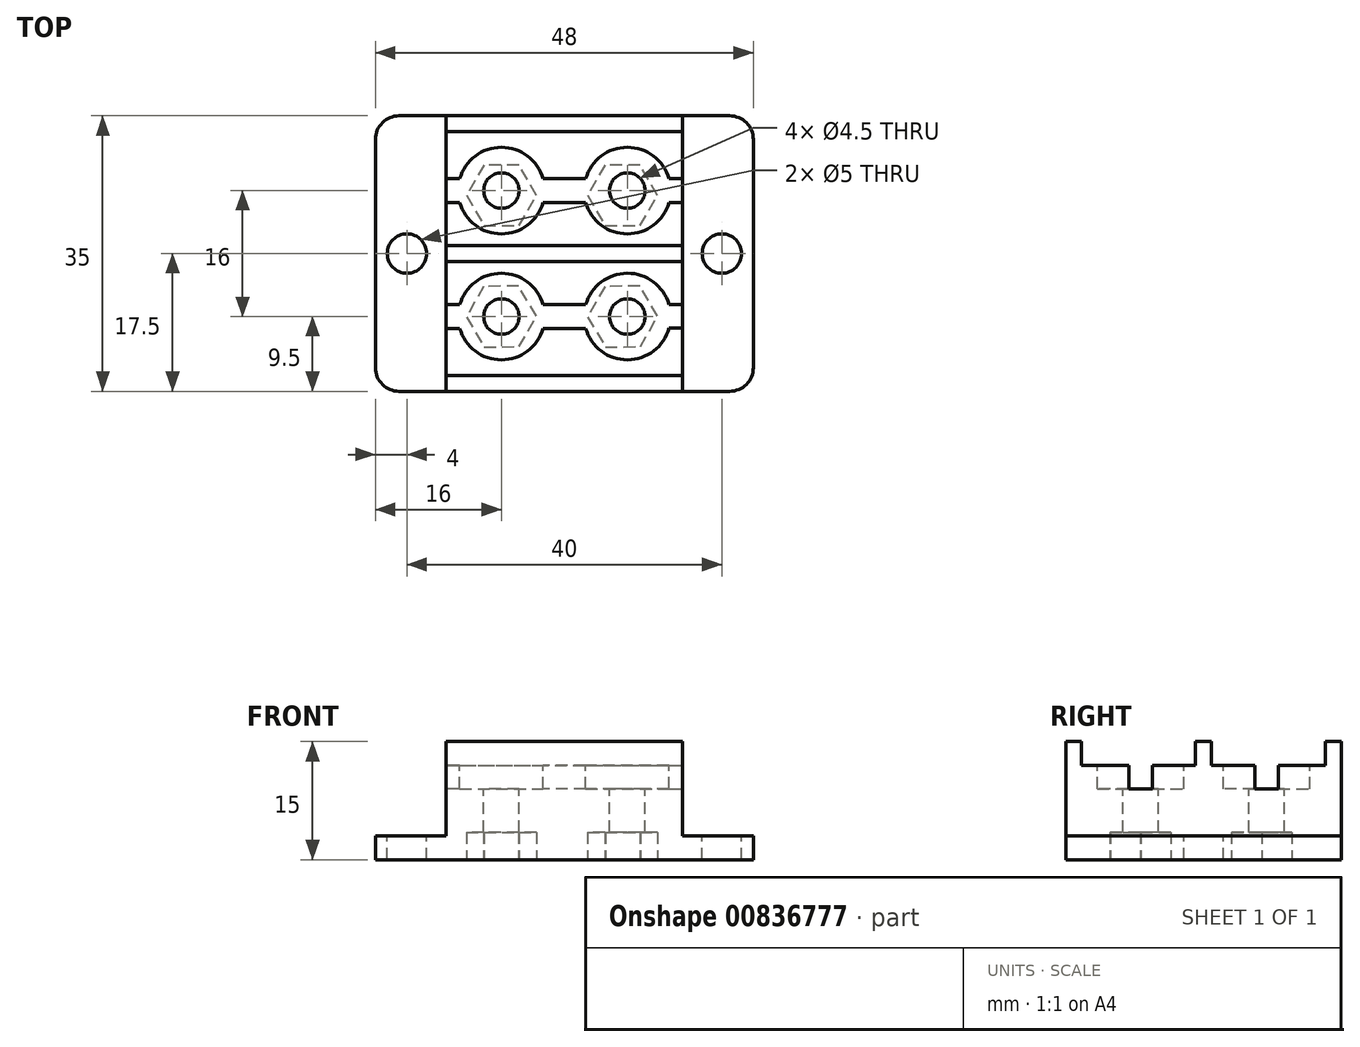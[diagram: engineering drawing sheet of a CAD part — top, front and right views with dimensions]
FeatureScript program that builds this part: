
annotation { "Feature Type Name" : "Feature", "Feature Type Description" : "" }
export const myFeature = defineFeature(function(context is Context, id is Id, definition is map)
    precondition{}
    {
        {
            var Q0;
            Q0=qCreatedBy(makeId("Front.planeOp"),FACE);
            var sketch = newSketch(context, id + "F0", { "sketchPlane" : qUnion([Q0])});
            skLineSegment(sketch, "E0", {"start": v(0, 0) * mm, "end": v(-9, 0) * mm});
            skLineSegment(sketch, "E1", {"start": v(-9, 0) * mm, "end": v(-9, 3) * mm});
            skLineSegment(sketch, "E2", {"start": v(-9, 3) * mm, "end": v(0, 3) * mm});
            skLineSegment(sketch, "E3", {"start": v(0, 3) * mm, "end": v(0, 12) * mm});
            skLineSegment(sketch, "E4", {"start": v(0, 12) * mm, "end": v(30, 12) * mm});
            skLineSegment(sketch, "E5", {"start": v(30, 12) * mm, "end": v(30, 3) * mm});
            skLineSegment(sketch, "E6", {"start": v(30, 3) * mm, "end": v(39, 3) * mm});
            skLineSegment(sketch, "E7", {"start": v(39, 3) * mm, "end": v(39, 0) * mm});
            skLineSegment(sketch, "E8", {"start": v(39, 0) * mm, "end": v(0, 0) * mm});
            skSolve(sketch);
        }
        {
            var Q0;
            Q0=makeQuery(id+"F0.imprint","IMPRINT",FACE,{"disambiguationData":[TD([[makeQuery(id+"F0.imprint","IMPRINT",EDGE,{"derivedFrom":sQuery(id+"F0.wireOp",EDGE,"E0")}),-1.0]])]});
            extrude(context, id + "F1", {"entities" : qUnion([Q0]), "oppositeDirection" : true, "depth" : 35 * mm, "offsetDistance" : 25 * mm});
        }
        {
            var Q0;
            Q0=qCreatedBy(makeId("Top.planeOp"),FACE);
            var Q1;
            Q1=makeQuery(id+"F1.opExtrude","CAP_VERTEX",VERTEX,{"disambiguationData":[OSD([sQuery(id+"F0.wireOp",EDGE,"E3"),sQuery(id+"F0.wireOp",EDGE,"E4")])],"isStart":false});
            cPlane(context, id + "F2", {"entities" : qUnion([Q0, Q1]), "cplaneType" : CPlaneType.PLANE_POINT, "offset" : 25 * mm, "width" : 150 * mm, "height" : 150 * mm});
        }
        {
            var Q0;
            Q0=qCreatedBy(id+"F2.planeOp",FACE);
            var sketch = newSketch(context, id + "F3", { "sketchPlane" : qUnion([Q0])});
            skLineSegment(sketch, "E9", {"start": v(23, 53.6) * mm, "end": v(23, -24.59) * mm, "construction": true});
            skLineSegment(sketch, "E10", {"start": v(7, 50.62) * mm, "end": v(7, -28.29) * mm, "construction": true});
            skLineSegment(sketch, "E11", {"start": v(23.6, 25.5) * mm, "end": v(1.01, 25.5) * mm, "construction": true});
            skLineSegment(sketch, "E12", {"start": v(28.02, 9.5) * mm, "end": v(4.88, 9.5) * mm, "construction": true});
            skCircle(sketch, "E13", {"center": v(23, 25.5) * mm, "radius": 2.25 * mm});
            skCircle(sketch, "E14", {"center": v(23, 9.5) * mm, "radius": 2.25 * mm});
            skCircle(sketch, "E15", {"center": v(7, 25.5) * mm, "radius": 2.25 * mm});
            skCircle(sketch, "E16", {"center": v(7, 9.5) * mm, "radius": 2.25 * mm});
            skLineSegment(sketch, "E17.bottom", {"start": v(29.45, 0) * mm, "end": v(0, 0) * mm});
            skLineSegment(sketch, "E18.bottom", {"start": v(8.68, 27) * mm, "end": v(21.32, 27) * mm});
            skLineSegment(sketch, "E18.top", {"start": v(8.68, 24) * mm, "end": v(21.32, 24) * mm});
            skLineSegment(sketch, "E18.left", {"start": v(8.68, 27) * mm, "end": v(8.68, 24) * mm});
            skLineSegment(sketch, "E18.right", {"start": v(21.32, 27) * mm, "end": v(21.32, 24) * mm});
            skLineSegment(sketch, "E19", {"start": v(8.68, 11) * mm, "end": v(21.32, 11) * mm});
            skLineSegment(sketch, "E20", {"start": v(21.32, 11) * mm, "end": v(21.32, 8) * mm});
            skLineSegment(sketch, "E21", {"start": v(21.32, 8) * mm, "end": v(8.68, 8) * mm});
            skLineSegment(sketch, "E22", {"start": v(8.68, 8) * mm, "end": v(8.68, 11) * mm});
            skCircle(sketch, "E23", {"center": v(7, 25.5) * mm, "radius": 5.5 * mm});
            skCircle(sketch, "E24", {"center": v(23, 25.5) * mm, "radius": 5.5 * mm});
            skCircle(sketch, "E25", {"center": v(7, 9.5) * mm, "radius": 5.5 * mm});
            skCircle(sketch, "E26", {"center": v(23, 9.5) * mm, "radius": 5.5 * mm});
            skLineSegment(sketch, "E27.bottom", {"start": v(28.3, 27) * mm, "end": v(30.07, 27) * mm});
            skLineSegment(sketch, "E28.bottom", {"start": v(5.32, 27) * mm, "end": v(0, 27) * mm});
            skLineSegment(sketch, "E28.top", {"start": v(5.32, 24) * mm, "end": v(0, 24) * mm});
            skLineSegment(sketch, "E28.left", {"start": v(5.32, 27) * mm, "end": v(5.32, 24) * mm});
            skLineSegment(sketch, "E28.right", {"start": v(0, 27) * mm, "end": v(0, 24) * mm});
            skLineSegment(sketch, "E29.bottom", {"start": v(24.68, 27) * mm, "end": v(30, 27) * mm});
            skLineSegment(sketch, "E29.top", {"start": v(24.68, 24) * mm, "end": v(30, 24) * mm});
            skLineSegment(sketch, "E29.left", {"start": v(24.68, 27) * mm, "end": v(24.68, 24) * mm});
            skLineSegment(sketch, "E29.right", {"start": v(30, 27) * mm, "end": v(30, 24) * mm});
            skLineSegment(sketch, "E30.bottom", {"start": v(5.32, 11) * mm, "end": v(0, 11) * mm});
            skLineSegment(sketch, "E30.top", {"start": v(5.32, 8) * mm, "end": v(0, 8) * mm});
            skLineSegment(sketch, "E30.left", {"start": v(5.32, 11) * mm, "end": v(5.32, 8) * mm});
            skLineSegment(sketch, "E30.right", {"start": v(0, 11) * mm, "end": v(0, 8) * mm});
            skLineSegment(sketch, "E31.bottom", {"start": v(24.64, 11.04) * mm, "end": v(30, 11.04) * mm});
            skLineSegment(sketch, "E31.top", {"start": v(24.64, 8.04) * mm, "end": v(30, 8.04) * mm});
            skLineSegment(sketch, "E31.left", {"start": v(24.64, 11.04) * mm, "end": v(24.64, 8.04) * mm});
            skLineSegment(sketch, "E31.right", {"start": v(30, 11.04) * mm, "end": v(30, 8.04) * mm});
            skSolve(sketch);
        }
        {
            var Q0;
            Q0=makeQuery(id+"F1.opExtrude","SWEPT_FACE",FACE,{"disambiguationData":[OSD([sQuery(id+"F0.wireOp",EDGE,"E6")])]});
            var sketch = newSketch(context, id + "F4", { "sketchPlane" : qUnion([Q0])});
            skCircle(sketch, "E32", {"center": v(-5, 17.5) * mm, "radius": 2.5 * mm});
            skCircle(sketch, "E33", {"center": v(35, 17.5) * mm, "radius": 2.5 * mm});
            skSolve(sketch);
        }
        {
            var Q0;
            Q0=makeQuery(id+"F4.imprint","IMPRINT",FACE,{"disambiguationData":[TD([[makeQuery(id+"F4.imprint","IMPRINT",EDGE,{"derivedFrom":sQuery(id+"F4.wireOp",EDGE,"E32")}),1.0]])]});
            var Q1;
            Q1=makeQuery(id+"F4.imprint","IMPRINT",FACE,{"disambiguationData":[TD([[makeQuery(id+"F4.imprint","IMPRINT",EDGE,{"derivedFrom":sQuery(id+"F4.wireOp",EDGE,"E33")}),1.0]])]});
            extrude(context, id + "F5", {"entities" : qUnion([Q0, Q1]), "operationType" : NewBodyOperationType.REMOVE, "endBound" : BoundingType.UP_TO_NEXT, "oppositeDirection" : true, "depth" : 25 * mm, "offsetDistance" : 25 * mm});
        }
        {
            var Q0;
            Q0=makeQuery(id+"F1.opExtrude","CAP_EDGE",EDGE,{"disambiguationData":[OSD([sQuery(id+"F0.wireOp",EDGE,"E1")])],"isStart":false});
            var Q1;
            Q1=makeQuery(id+"F1.opExtrude","CAP_EDGE",EDGE,{"disambiguationData":[OSD([sQuery(id+"F0.wireOp",EDGE,"E7")])],"isStart":false});
            var Q2;
            Q2=makeQuery(id+"F1.opExtrude","CAP_EDGE",EDGE,{"disambiguationData":[OSD([sQuery(id+"F0.wireOp",EDGE,"E7")])],"isStart":true});
            var Q3;
            Q3=makeQuery(id+"F1.opExtrude","CAP_EDGE",EDGE,{"disambiguationData":[OSD([sQuery(id+"F0.wireOp",EDGE,"E1")])],"isStart":true});
            fillet(context, id + "F6", {"entities" : qUnion([Q0, Q1, Q2, Q3]), "radius" : 3 * mm, "tangentPropagation" : true, "allowEdgeOverflow" : false});
        }
        {
            var Q0;
            Q0=makeQuery(id+"F1.opExtrude","SWEPT_FACE",FACE,{"disambiguationData":[OSD([sQuery(id+"F0.wireOp",EDGE,"E4")])]});
            var sketch = newSketch(context, id + "F7", { "sketchPlane" : qUnion([Q0])});
            skLineSegment(sketch, "E34.bottom", {"start": v(0, 35) * mm, "end": v(30, 35) * mm});
            skLineSegment(sketch, "E34.top", {"start": v(0, 33) * mm, "end": v(30, 33) * mm});
            skLineSegment(sketch, "E34.left", {"start": v(0, 35) * mm, "end": v(0, 33) * mm});
            skLineSegment(sketch, "E34.right", {"start": v(30, 35) * mm, "end": v(30, 33) * mm});
            skLineSegment(sketch, "E35.bottom", {"start": v(0, 18.5) * mm, "end": v(30, 18.5) * mm});
            skLineSegment(sketch, "E35.top", {"start": v(0, 16.5) * mm, "end": v(30, 16.5) * mm});
            skLineSegment(sketch, "E35.left", {"start": v(0, 18.5) * mm, "end": v(0, 16.5) * mm});
            skLineSegment(sketch, "E35.right", {"start": v(30, 18.5) * mm, "end": v(30, 16.5) * mm});
            skLineSegment(sketch, "E36.bottom", {"start": v(0, 0) * mm, "end": v(30, 0) * mm});
            skLineSegment(sketch, "E36.top", {"start": v(0, 2) * mm, "end": v(30, 2) * mm});
            skLineSegment(sketch, "E36.left", {"start": v(0, 0) * mm, "end": v(0, 2) * mm});
            skLineSegment(sketch, "E36.right", {"start": v(30, 0) * mm, "end": v(30, 2) * mm});
            skSolve(sketch);
        }
        {
            var Q0;
            Q0=makeQuery(id+"F7.imprint","IMPRINT",FACE,{"disambiguationData":[TD([[makeQuery(id+"F7.imprint","IMPRINT",EDGE,{"derivedFrom":sQuery(id+"F7.wireOp",EDGE,"E34.bottom")}),-1.0]])]});
            var Q1;
            Q1=makeQuery(id+"F7.imprint","IMPRINT",FACE,{"disambiguationData":[TD([[makeQuery(id+"F7.imprint","IMPRINT",EDGE,{"derivedFrom":sQuery(id+"F7.wireOp",EDGE,"E35.bottom")}),-1.0]])]});
            var Q2;
            Q2=makeQuery(id+"F7.imprint","IMPRINT",FACE,{"disambiguationData":[TD([[makeQuery(id+"F7.imprint","IMPRINT",EDGE,{"derivedFrom":sQuery(id+"F7.wireOp",EDGE,"E36.bottom")}),1.0]])]});
            extrude(context, id + "F8", {"entities" : qUnion([Q0, Q1, Q2]), "operationType" : NewBodyOperationType.ADD, "depth" : 3 * mm, "offsetDistance" : 25 * mm});
        }
        {
            var Q0;
            {var subQ0=sQuery(id+"F3.wireOp",EDGE,"E18.left");Q0=makeQuery(id+"F3.imprint","IMPRINT",FACE,{"disambiguationData":[TD([[makeQuery(id+"F3.imprint","IMPRINT",EDGE,{"derivedFrom":subQ0}),-1.0]])]});}
            var Q1;
            {var subQ0=sQuery(id+"F3.wireOp",EDGE,"E28.left");Q1=makeQuery(id+"F3.imprint","IMPRINT",FACE,{"disambiguationData":[TD([[makeQuery(id+"F3.imprint","IMPRINT",EDGE,{"derivedFrom":subQ0}),-1.0]])]});}
            var Q2;
            {var subQ0=sQuery(id+"F3.wireOp",EDGE,"E18.left");Q2=makeQuery(id+"F3.imprint","IMPRINT",FACE,{"disambiguationData":[TD([[makeQuery(id+"F3.imprint","IMPRINT",EDGE,{"derivedFrom":subQ0}),1.0]])]});}
            var Q3;
            {var subQ0=sQuery(id+"F3.wireOp",EDGE,"E18.right");Q3=makeQuery(id+"F3.imprint","IMPRINT",FACE,{"disambiguationData":[TD([[makeQuery(id+"F3.imprint","IMPRINT",EDGE,{"derivedFrom":subQ0}),-1.0]])]});}
            var Q4;
            {var subQ0=sQuery(id+"F3.wireOp",EDGE,"E29.left");Q4=makeQuery(id+"F3.imprint","IMPRINT",FACE,{"disambiguationData":[TD([[makeQuery(id+"F3.imprint","IMPRINT",EDGE,{"derivedFrom":subQ0}),1.0]])]});}
            var Q5;
            {var subQ0=sQuery(id+"F3.wireOp",EDGE,"E18.right");Q5=makeQuery(id+"F3.imprint","IMPRINT",FACE,{"disambiguationData":[TD([[makeQuery(id+"F3.imprint","IMPRINT",EDGE,{"derivedFrom":subQ0}),1.0]])]});}
            var Q6;
            {var subQ0=sQuery(id+"F3.wireOp",EDGE,"E22");Q6=makeQuery(id+"F3.imprint","IMPRINT",FACE,{"disambiguationData":[TD([[makeQuery(id+"F3.imprint","IMPRINT",EDGE,{"derivedFrom":subQ0}),1.0]])]});}
            var Q7;
            {var subQ0=sQuery(id+"F3.wireOp",EDGE,"E22");Q7=makeQuery(id+"F3.imprint","IMPRINT",FACE,{"disambiguationData":[TD([[makeQuery(id+"F3.imprint","IMPRINT",EDGE,{"derivedFrom":subQ0}),-1.0]])]});}
            var Q8;
            {var subQ0=sQuery(id+"F3.wireOp",EDGE,"E30.left");Q8=makeQuery(id+"F3.imprint","IMPRINT",FACE,{"disambiguationData":[TD([[makeQuery(id+"F3.imprint","IMPRINT",EDGE,{"derivedFrom":subQ0}),-1.0]])]});}
            var Q9;
            {var subQ0=sQuery(id+"F3.wireOp",EDGE,"E20");Q9=makeQuery(id+"F3.imprint","IMPRINT",FACE,{"disambiguationData":[TD([[makeQuery(id+"F3.imprint","IMPRINT",EDGE,{"derivedFrom":subQ0}),-1.0]])]});}
            var Q10;
            {var subQ0=sQuery(id+"F3.wireOp",EDGE,"E31.left");Q10=makeQuery(id+"F3.imprint","IMPRINT",FACE,{"disambiguationData":[TD([[makeQuery(id+"F3.imprint","IMPRINT",EDGE,{"derivedFrom":subQ0}),1.0]])]});}
            var Q11;
            {var subQ4=sQuery(id+"F3.wireOp",EDGE,"E20");Q11=makeQuery(id+"F3.imprint","IMPRINT",FACE,{"disambiguationData":[TD([[makeQuery(id+"F3.imprint","IMPRINT",EDGE,{"derivedFrom":subQ4}),1.0]])]});}
            extrude(context, id + "F9", {"entities" : qUnion([Q0, Q1, Q2, Q3, Q4, Q5, Q6, Q7, Q8, Q9, Q10, Q11]), "operationType" : NewBodyOperationType.REMOVE, "endBound" : BoundingType.UP_TO_NEXT, "oppositeDirection" : true, "depth" : 25 * mm, "offsetDistance" : 25 * mm});
        }
        {
            var Q0;
            {var subQ0=sQuery(id+"F3.wireOp",EDGE,"E21");var subQ5=sQuery(id+"F3.wireOp",EDGE,"E25");var subQ6=makeQuery(id+"F3.imprint","INTERSECT",VERTEX,{"derivedFrom":[subQ0,subQ5]});Q0=makeQuery(id+"F3.imprint","IMPRINT",FACE,{"disambiguationData":[TD([[makeQuery(id+"F3.imprint","IMPRINT",EDGE,{"disambiguationData":[TD([[subQ6,1.0]])],"derivedFrom":subQ5}),1.0]])]});}
            var Q1;
            {var subQ1=sQuery(id+"F3.wireOp",EDGE,"E30.bottom");var subQ6=sQuery(id+"F3.wireOp",EDGE,"E25");var subQ7=makeQuery(id+"F3.imprint","INTERSECT",VERTEX,{"derivedFrom":[subQ6,subQ1]});Q1=makeQuery(id+"F3.imprint","IMPRINT",FACE,{"disambiguationData":[TD([[makeQuery(id+"F3.imprint","IMPRINT",EDGE,{"disambiguationData":[TD([[subQ7,-1.0]])],"derivedFrom":subQ6}),1.0]])]});}
            var Q2;
            {var subQ0=sQuery(id+"F3.wireOp",EDGE,"E19");var subQ5=sQuery(id+"F3.wireOp",EDGE,"E25");var subQ6=makeQuery(id+"F3.imprint","INTERSECT",VERTEX,{"derivedFrom":[subQ0,subQ5]});Q2=makeQuery(id+"F3.imprint","IMPRINT",FACE,{"disambiguationData":[TD([[makeQuery(id+"F3.imprint","IMPRINT",EDGE,{"disambiguationData":[TD([[subQ6,-1.0]])],"derivedFrom":subQ5}),1.0]])]});}
            var Q3;
            {var subQ1=sQuery(id+"F3.wireOp",EDGE,"E19");var subQ6=sQuery(id+"F3.wireOp",EDGE,"E25");var subQ8=makeQuery(id+"F3.imprint","INTERSECT",VERTEX,{"derivedFrom":[subQ1,subQ6]});Q3=makeQuery(id+"F3.imprint","IMPRINT",FACE,{"disambiguationData":[TD([[makeQuery(id+"F3.imprint","IMPRINT",EDGE,{"disambiguationData":[TD([[subQ8,1.0]])],"derivedFrom":subQ6}),1.0]])]});}
            var Q4;
            {var subQ0=sQuery(id+"F3.wireOp",EDGE,"E19");var subQ5=sQuery(id+"F3.wireOp",EDGE,"E26");var subQ6=makeQuery(id+"F3.imprint","INTERSECT",VERTEX,{"derivedFrom":[subQ0,subQ5]});Q4=makeQuery(id+"F3.imprint","IMPRINT",FACE,{"disambiguationData":[TD([[makeQuery(id+"F3.imprint","IMPRINT",EDGE,{"disambiguationData":[TD([[subQ6,1.0]])],"derivedFrom":subQ5}),1.0]])]});}
            var Q5;
            {var subQ1=sQuery(id+"F3.wireOp",EDGE,"E19");var subQ6=sQuery(id+"F3.wireOp",EDGE,"E26");var subQ7=makeQuery(id+"F3.imprint","INTERSECT",VERTEX,{"derivedFrom":[subQ1,subQ6]});Q5=makeQuery(id+"F3.imprint","IMPRINT",FACE,{"disambiguationData":[TD([[makeQuery(id+"F3.imprint","IMPRINT",EDGE,{"disambiguationData":[TD([[subQ7,-1.0]])],"derivedFrom":subQ6}),1.0]])]});}
            var Q6;
            {var subQ0=sQuery(id+"F3.wireOp",EDGE,"E21");var subQ5=sQuery(id+"F3.wireOp",EDGE,"E26");var subQ6=makeQuery(id+"F3.imprint","INTERSECT",VERTEX,{"derivedFrom":[subQ0,subQ5]});Q6=makeQuery(id+"F3.imprint","IMPRINT",FACE,{"disambiguationData":[TD([[makeQuery(id+"F3.imprint","IMPRINT",EDGE,{"disambiguationData":[TD([[subQ6,-1.0]])],"derivedFrom":subQ5}),1.0]])]});}
            var Q7;
            {var subQ0=sQuery(id+"F3.wireOp",EDGE,"E31.bottom");var subQ5=sQuery(id+"F3.wireOp",EDGE,"E26");var subQ6=makeQuery(id+"F3.imprint","INTERSECT",VERTEX,{"derivedFrom":[subQ5,subQ0]});Q7=makeQuery(id+"F3.imprint","IMPRINT",FACE,{"disambiguationData":[TD([[makeQuery(id+"F3.imprint","IMPRINT",EDGE,{"disambiguationData":[TD([[subQ6,1.0]])],"derivedFrom":subQ5}),1.0]])]});}
            var Q8;
            {var subQ0=sQuery(id+"F3.wireOp",EDGE,"E18.top");var subQ5=sQuery(id+"F3.wireOp",EDGE,"E24");var subQ6=makeQuery(id+"F3.imprint","INTERSECT",VERTEX,{"derivedFrom":[subQ0,subQ5]});Q8=makeQuery(id+"F3.imprint","IMPRINT",FACE,{"disambiguationData":[TD([[makeQuery(id+"F3.imprint","IMPRINT",EDGE,{"disambiguationData":[TD([[subQ6,-1.0]])],"derivedFrom":subQ5}),1.0]])]});}
            var Q9;
            {var subQ1=sQuery(id+"F3.wireOp",EDGE,"E29.bottom");var subQ6=sQuery(id+"F3.wireOp",EDGE,"E24");var subQ7=makeQuery(id+"F3.imprint","INTERSECT",VERTEX,{"derivedFrom":[subQ6,subQ1]});Q9=makeQuery(id+"F3.imprint","IMPRINT",FACE,{"disambiguationData":[TD([[makeQuery(id+"F3.imprint","IMPRINT",EDGE,{"disambiguationData":[TD([[subQ7,1.0]])],"derivedFrom":subQ6}),1.0]])]});}
            var Q10;
            {var subQ0=sQuery(id+"F3.wireOp",EDGE,"E18.bottom");var subQ5=sQuery(id+"F3.wireOp",EDGE,"E24");var subQ6=makeQuery(id+"F3.imprint","INTERSECT",VERTEX,{"derivedFrom":[subQ0,subQ5]});Q10=makeQuery(id+"F3.imprint","IMPRINT",FACE,{"disambiguationData":[TD([[makeQuery(id+"F3.imprint","IMPRINT",EDGE,{"disambiguationData":[TD([[subQ6,1.0]])],"derivedFrom":subQ5}),1.0]])]});}
            var Q11;
            {var subQ1=sQuery(id+"F3.wireOp",EDGE,"E18.bottom");var subQ6=sQuery(id+"F3.wireOp",EDGE,"E24");var subQ8=makeQuery(id+"F3.imprint","INTERSECT",VERTEX,{"derivedFrom":[subQ1,subQ6]});Q11=makeQuery(id+"F3.imprint","IMPRINT",FACE,{"disambiguationData":[TD([[makeQuery(id+"F3.imprint","IMPRINT",EDGE,{"disambiguationData":[TD([[subQ8,-1.0]])],"derivedFrom":subQ6}),1.0]])]});}
            var Q12;
            {var subQ0=sQuery(id+"F3.wireOp",EDGE,"E18.top");var subQ5=sQuery(id+"F3.wireOp",EDGE,"E23");var subQ7=makeQuery(id+"F3.imprint","INTERSECT",VERTEX,{"derivedFrom":[subQ0,subQ5]});Q12=makeQuery(id+"F3.imprint","IMPRINT",FACE,{"disambiguationData":[TD([[makeQuery(id+"F3.imprint","IMPRINT",EDGE,{"disambiguationData":[TD([[subQ7,1.0]])],"derivedFrom":subQ5}),1.0]])]});}
            var Q13;
            {var subQ0=sQuery(id+"F3.wireOp",EDGE,"E18.bottom");var subQ5=sQuery(id+"F3.wireOp",EDGE,"E23");var subQ7=makeQuery(id+"F3.imprint","INTERSECT",VERTEX,{"derivedFrom":[subQ0,subQ5]});Q13=makeQuery(id+"F3.imprint","IMPRINT",FACE,{"disambiguationData":[TD([[makeQuery(id+"F3.imprint","IMPRINT",EDGE,{"disambiguationData":[TD([[subQ7,-1.0]])],"derivedFrom":subQ5}),1.0]])]});}
            var Q14;
            {var subQ1=sQuery(id+"F3.wireOp",EDGE,"E18.bottom");var subQ6=sQuery(id+"F3.wireOp",EDGE,"E23");var subQ7=makeQuery(id+"F3.imprint","INTERSECT",VERTEX,{"derivedFrom":[subQ1,subQ6]});Q14=makeQuery(id+"F3.imprint","IMPRINT",FACE,{"disambiguationData":[TD([[makeQuery(id+"F3.imprint","IMPRINT",EDGE,{"disambiguationData":[TD([[subQ7,1.0]])],"derivedFrom":subQ6}),1.0]])]});}
            var Q15;
            {var subQ1=sQuery(id+"F3.wireOp",EDGE,"E28.bottom");var subQ6=sQuery(id+"F3.wireOp",EDGE,"E23");var subQ7=makeQuery(id+"F3.imprint","INTERSECT",VERTEX,{"derivedFrom":[subQ6,subQ1]});Q15=makeQuery(id+"F3.imprint","IMPRINT",FACE,{"disambiguationData":[TD([[makeQuery(id+"F3.imprint","IMPRINT",EDGE,{"disambiguationData":[TD([[subQ7,-1.0]])],"derivedFrom":subQ6}),1.0]])]});}
            extrude(context, id + "F10", {"entities" : qUnion([Q0, Q1, Q2, Q3, Q4, Q5, Q6, Q7, Q8, Q9, Q10, Q11, Q12, Q13, Q14, Q15]), "operationType" : NewBodyOperationType.REMOVE, "oppositeDirection" : true, "depth" : 3 * mm, "offsetDistance" : 25 * mm});
        }
        {
            var Q0;
            Q0=qSketchRegion(id+"F3",true);
            extrude(context, id + "F11", {"entities" : qUnion([Q0]), "operationType" : NewBodyOperationType.REMOVE, "oppositeDirection" : true, "depth" : 3 * mm, "offsetDistance" : 25 * mm});
        }
        {
            var Q0;
            Q0=makeQuery(id+"F1.opExtrude","SWEPT_FACE",FACE,{"disambiguationData":[OSD([sQuery(id+"F0.wireOp",EDGE,"E0"),sQuery(id+"F0.wireOp",EDGE,"E8")])]});
            var sketch = newSketch(context, id + "F12", { "sketchPlane" : qUnion([Q0])});
            skCircle(sketch, "E37.cCircle", {"center": v(7, -9.5) * mm, "radius": 3.85 * mm, "construction": true});
            skLineSegment(sketch, "E37.0", {"start": v(11.45, -9.54) * mm, "end": v(9.2, -13.37) * mm});
            skLineSegment(sketch, "E37.1", {"start": v(9.2, -13.37) * mm, "end": v(4.75, -13.33) * mm});
            skLineSegment(sketch, "E37.2", {"start": v(4.75, -13.33) * mm, "end": v(2.55, -9.46) * mm});
            skLineSegment(sketch, "E37.3", {"start": v(2.55, -9.46) * mm, "end": v(4.8, -5.63) * mm});
            skLineSegment(sketch, "E37.4", {"start": v(4.8, -5.63) * mm, "end": v(9.25, -5.67) * mm});
            skLineSegment(sketch, "E37.5", {"start": v(9.25, -5.67) * mm, "end": v(11.45, -9.54) * mm});
            skPoint(sketch, "E37.0.midPoint", {"position": v(10.32, -11.45) * mm});
            skCircle(sketch, "E38.cCircle", {"center": v(22.4, -9.5) * mm, "radius": 3.85 * mm, "construction": true});
            skLineSegment(sketch, "E38.0", {"start": v(26.85, -9.54) * mm, "end": v(24.6, -13.37) * mm});
            skLineSegment(sketch, "E38.1", {"start": v(24.6, -13.37) * mm, "end": v(20.15, -13.33) * mm});
            skLineSegment(sketch, "E38.2", {"start": v(20.15, -13.33) * mm, "end": v(17.95, -9.46) * mm});
            skLineSegment(sketch, "E38.3", {"start": v(17.95, -9.46) * mm, "end": v(20.2, -5.63) * mm});
            skLineSegment(sketch, "E38.4", {"start": v(20.2, -5.63) * mm, "end": v(24.65, -5.67) * mm});
            skLineSegment(sketch, "E38.5", {"start": v(24.65, -5.67) * mm, "end": v(26.85, -9.54) * mm});
            skPoint(sketch, "E38.0.midPoint", {"position": v(25.72, -11.45) * mm});
            skCircle(sketch, "E39.cCircle", {"center": v(7, -24.9) * mm, "radius": 3.85 * mm, "construction": true});
            skLineSegment(sketch, "E39.0", {"start": v(11.45, -24.9) * mm, "end": v(9.22, -28.75) * mm});
            skLineSegment(sketch, "E39.1", {"start": v(9.22, -28.75) * mm, "end": v(4.78, -28.75) * mm});
            skLineSegment(sketch, "E39.2", {"start": v(4.78, -28.75) * mm, "end": v(2.55, -24.9) * mm});
            skLineSegment(sketch, "E39.3", {"start": v(2.55, -24.9) * mm, "end": v(4.78, -21.05) * mm});
            skLineSegment(sketch, "E39.4", {"start": v(4.78, -21.05) * mm, "end": v(9.22, -21.05) * mm});
            skLineSegment(sketch, "E39.5", {"start": v(9.22, -21.05) * mm, "end": v(11.45, -24.9) * mm});
            skPoint(sketch, "E39.0.midPoint", {"position": v(10.33, -26.82) * mm});
            skCircle(sketch, "E40.cCircle", {"center": v(22.4, -24.9) * mm, "radius": 3.85 * mm, "construction": true});
            skLineSegment(sketch, "E40.0", {"start": v(26.85, -24.9) * mm, "end": v(24.62, -28.75) * mm});
            skLineSegment(sketch, "E40.1", {"start": v(24.62, -28.75) * mm, "end": v(20.18, -28.75) * mm});
            skLineSegment(sketch, "E40.2", {"start": v(20.18, -28.75) * mm, "end": v(17.95, -24.9) * mm});
            skLineSegment(sketch, "E40.3", {"start": v(17.95, -24.9) * mm, "end": v(20.18, -21.05) * mm});
            skLineSegment(sketch, "E40.4", {"start": v(20.18, -21.05) * mm, "end": v(24.62, -21.05) * mm});
            skLineSegment(sketch, "E40.5", {"start": v(24.62, -21.05) * mm, "end": v(26.85, -24.9) * mm});
            skPoint(sketch, "E40.0.midPoint", {"position": v(25.73, -26.82) * mm});
            skSolve(sketch);
        }
        {
            var Q0;
            Q0=makeQuery(id+"F12.imprint","IMPRINT",FACE,{"disambiguationData":[TD([[makeQuery(id+"F12.imprint","IMPRINT",EDGE,{"derivedFrom":sQuery(id+"F12.wireOp",EDGE,"E37.0")}),-1.0]])]});
            var Q1;
            Q1=makeQuery(id+"F12.imprint","IMPRINT",FACE,{"disambiguationData":[TD([[makeQuery(id+"F12.imprint","IMPRINT",EDGE,{"derivedFrom":sQuery(id+"F12.wireOp",EDGE,"E38.0")}),-1.0]])]});
            var Q2;
            Q2=makeQuery(id+"F12.imprint","IMPRINT",FACE,{"disambiguationData":[TD([[makeQuery(id+"F12.imprint","IMPRINT",EDGE,{"derivedFrom":sQuery(id+"F12.wireOp",EDGE,"E40.0")}),-1.0]])]});
            var Q3;
            Q3=makeQuery(id+"F12.imprint","IMPRINT",FACE,{"disambiguationData":[TD([[makeQuery(id+"F12.imprint","IMPRINT",EDGE,{"derivedFrom":sQuery(id+"F12.wireOp",EDGE,"E39.0")}),-1.0]])]});
            extrude(context, id + "F13", {"entities" : qUnion([Q0, Q1, Q2, Q3]), "operationType" : NewBodyOperationType.REMOVE, "oppositeDirection" : true, "depth" : 3.5 * mm, "offsetDistance" : 25 * mm});
        }
    });
